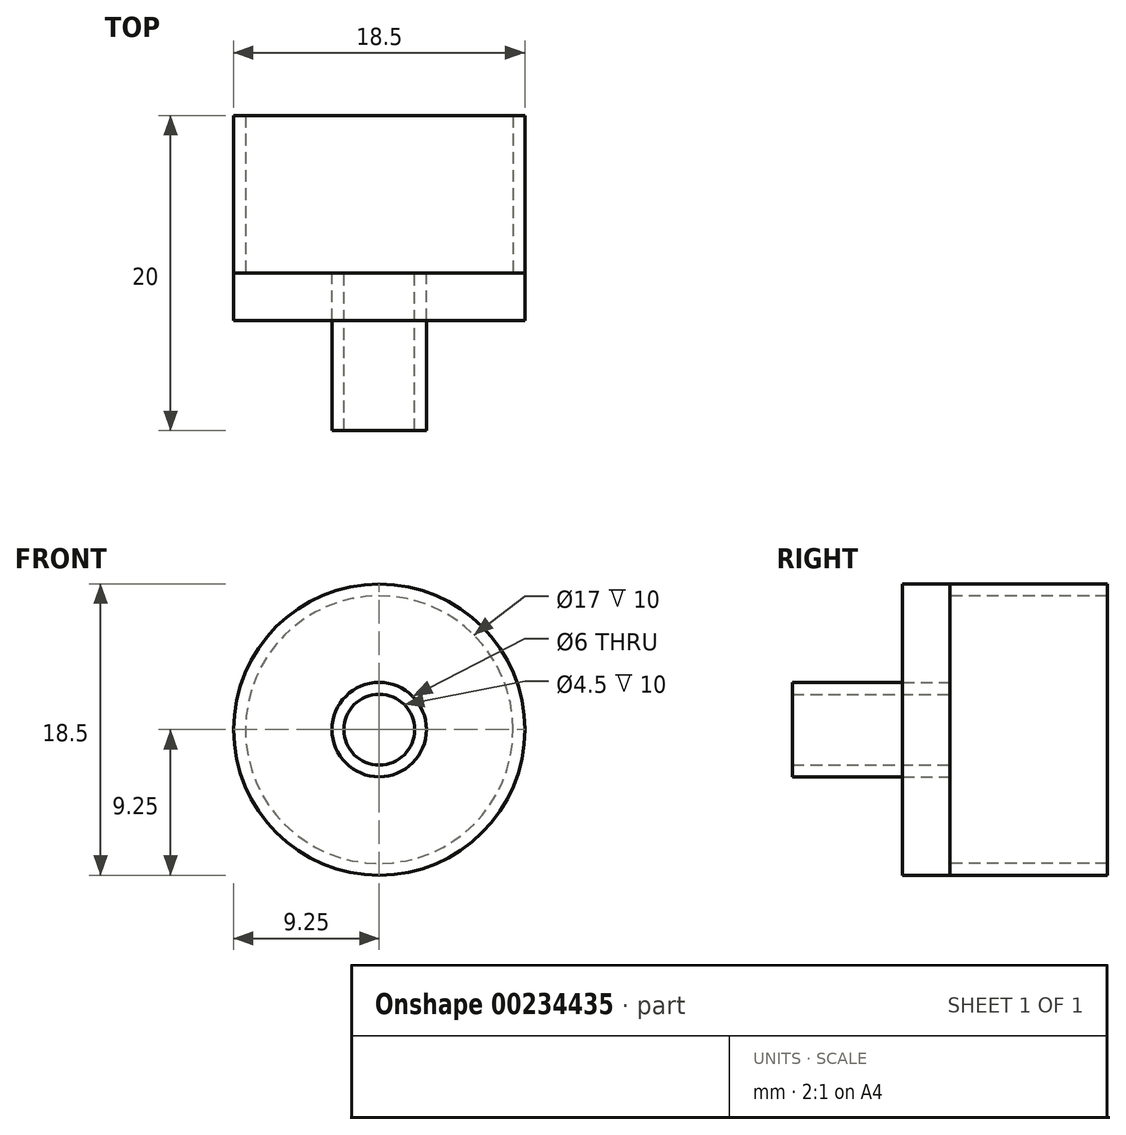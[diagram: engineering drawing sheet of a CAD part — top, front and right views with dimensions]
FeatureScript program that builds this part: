
annotation { "Feature Type Name" : "Feature", "Feature Type Description" : "" }
export const myFeature = defineFeature(function(context is Context, id is Id, definition is map)
    precondition{}
    {
        {
            var Q0;
            Q0=qCreatedBy(makeId("Front.planeOp"),FACE);
            var sketch = newSketch(context, id + "F0", { "sketchPlane" : qUnion([Q0])});
            skCircle(sketch, "E0", {"center": v(0, 0) * mm, "radius": 3 * mm});
            skCircle(sketch, "E1", {"center": v(0, 0) * mm, "radius": 2.25 * mm});
            skSolve(sketch);
        }
        {
            var Q0;
            Q0=qSketchRegion(id+"F0",true);
            extrude(context, id + "F1", {"entities" : qUnion([Q0]), "depth" : 10 * mm});
        }
        {
            var Q0;
            Q0=qCreatedBy(makeId("Front.planeOp"),FACE);
            var sketch = newSketch(context, id + "F2", { "sketchPlane" : qUnion([Q0])});
            skCircle(sketch, "E2", {"center": v(0, 0) * mm, "radius": 9.25 * mm});
            skCircle(sketch, "E3", {"center": v(0, 0) * mm, "radius": 3 * mm});
            skSolve(sketch);
        }
        {
            var Q0;
            Q0=qSketchRegion(id+"F2",true);
            extrude(context, id + "F3", {"entities" : qUnion([Q0]), "depth" : 3 * mm});
        }
        {
            var Q0;
            Q0=makeQuery(id+"F3.opExtrude","CAP_FACE",FACE,{"disambiguationData":[OSD([sQuery(id+"F2.wireOp",EDGE,"E2"),sQuery(id+"F2.wireOp",EDGE,"E3")])],"isStart":true});
            var sketch = newSketch(context, id + "F4", { "sketchPlane" : qUnion([Q0])});
            skCircle(sketch, "E4.0", {"center": v(0, 0) * mm, "radius": 8.5 * mm});
            skCircle(sketch, "E5", {"center": v(0, 0) * mm, "radius": 9.25 * mm});
            skSolve(sketch);
        }
        {
            var Q0;
            Q0=qSketchRegion(id+"F4",true);
            extrude(context, id + "F5", {"entities" : qUnion([Q0]), "depth" : 10 * mm});
        }
    });
